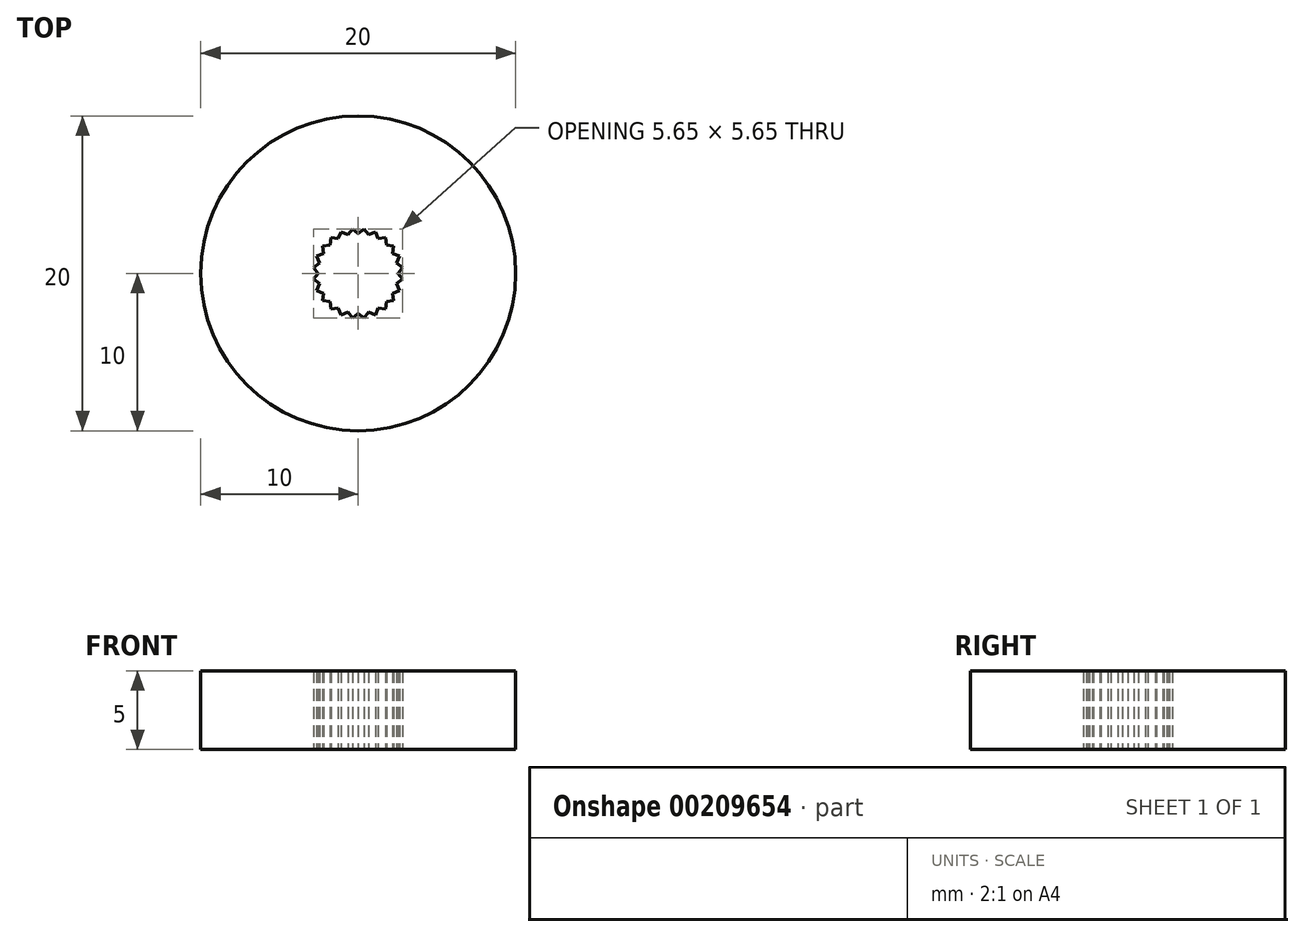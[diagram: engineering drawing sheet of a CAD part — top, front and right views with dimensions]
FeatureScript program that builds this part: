
annotation { "Feature Type Name" : "Feature", "Feature Type Description" : "" }
export const myFeature = defineFeature(function(context is Context, id is Id, definition is map)
    precondition{}
    {
        {
            var Q0;
            Q0=qCreatedBy(makeId("Top.planeOp"),FACE);
            var sketch = newSketch(context, id + "F0", { "sketchPlane" : qUnion([Q0])});
            skPoint(sketch, "E0", {"position": v(0, 2.54) * mm});
            skPoint(sketch, "E1", {"position": v(0.37, 2.83) * mm});
            skLineSegment(sketch, "E2", {"start": v(0, 2.54) * mm, "end": v(0.37, 2.83) * mm});
            skLineSegment(sketch, "E3", {"start": v(0, 2.54) * mm, "end": v(-0.37, 2.83) * mm});
            skLineSegment(sketch, "E4", {"start": v(0.37, 2.83) * mm, "end": v(0.66, 2.45) * mm});
            skLineSegment(sketch, "E5", {"start": v(0.66, 2.45) * mm, "end": v(1.1, 2.63) * mm});
            skLineSegment(sketch, "E6", {"start": v(1.27, 2.2) * mm, "end": v(1.1, 2.63) * mm});
            skLineSegment(sketch, "E7", {"start": v(1.73, 2.26) * mm, "end": v(1.27, 2.2) * mm});
            skLineSegment(sketch, "E8", {"start": v(1.8, 1.8) * mm, "end": v(1.73, 2.26) * mm});
            skLineSegment(sketch, "E9", {"start": v(2.26, 1.73) * mm, "end": v(1.8, 1.8) * mm});
            skLineSegment(sketch, "E10", {"start": v(2.2, 1.27) * mm, "end": v(2.26, 1.73) * mm});
            skLineSegment(sketch, "E11", {"start": v(2.2, 1.27) * mm, "end": v(2.63, 1.1) * mm});
            skLineSegment(sketch, "E12", {"start": v(2.63, 1.1) * mm, "end": v(2.45, 0.66) * mm});
            skLineSegment(sketch, "E13", {"start": v(2.45, 0.66) * mm, "end": v(2.83, 0.37) * mm});
            skLineSegment(sketch, "E14", {"start": v(2.83, 0.37) * mm, "end": v(2.54, 0) * mm});
            skLineSegment(sketch, "E15", {"start": v(2.54, 0) * mm, "end": v(2.83, -0.37) * mm});
            skLineSegment(sketch, "E16", {"start": v(2.83, -0.37) * mm, "end": v(2.45, -0.66) * mm});
            skLineSegment(sketch, "E17", {"start": v(2.45, -0.66) * mm, "end": v(2.63, -1.1) * mm});
            skLineSegment(sketch, "E18", {"start": v(2.63, -1.1) * mm, "end": v(2.2, -1.27) * mm});
            skLineSegment(sketch, "E19", {"start": v(2.2, -1.27) * mm, "end": v(2.26, -1.73) * mm});
            skLineSegment(sketch, "E20", {"start": v(2.26, -1.73) * mm, "end": v(1.8, -1.8) * mm});
            skLineSegment(sketch, "E21", {"start": v(1.8, -1.8) * mm, "end": v(1.73, -2.26) * mm});
            skLineSegment(sketch, "E22", {"start": v(1.73, -2.26) * mm, "end": v(1.27, -2.2) * mm});
            skLineSegment(sketch, "E23", {"start": v(1.27, -2.2) * mm, "end": v(1.1, -2.63) * mm});
            skLineSegment(sketch, "E24", {"start": v(1.1, -2.63) * mm, "end": v(0.66, -2.45) * mm});
            skLineSegment(sketch, "E25", {"start": v(0.66, -2.45) * mm, "end": v(0.37, -2.83) * mm});
            skLineSegment(sketch, "E26", {"start": v(0.37, -2.83) * mm, "end": v(0, -2.54) * mm});
            skLineSegment(sketch, "E27", {"start": v(0, -2.54) * mm, "end": v(-0.37, -2.83) * mm});
            skLineSegment(sketch, "E28", {"start": v(-0.37, -2.83) * mm, "end": v(-0.66, -2.45) * mm});
            skLineSegment(sketch, "E29", {"start": v(-0.66, -2.45) * mm, "end": v(-1.1, -2.63) * mm});
            skLineSegment(sketch, "E30", {"start": v(-1.1, -2.63) * mm, "end": v(-1.27, -2.2) * mm});
            skLineSegment(sketch, "E31", {"start": v(-1.27, -2.2) * mm, "end": v(-1.73, -2.26) * mm});
            skLineSegment(sketch, "E32", {"start": v(-1.73, -2.26) * mm, "end": v(-1.8, -1.8) * mm});
            skLineSegment(sketch, "E33", {"start": v(-1.8, -1.8) * mm, "end": v(-2.26, -1.73) * mm});
            skLineSegment(sketch, "E34", {"start": v(-2.26, -1.73) * mm, "end": v(-2.2, -1.27) * mm});
            skLineSegment(sketch, "E35", {"start": v(-2.63, -1.1) * mm, "end": v(-2.2, -1.27) * mm});
            skLineSegment(sketch, "E36", {"start": v(-2.63, -1.1) * mm, "end": v(-2.45, -0.66) * mm});
            skLineSegment(sketch, "E37", {"start": v(-2.45, -0.66) * mm, "end": v(-2.83, -0.37) * mm});
            skLineSegment(sketch, "E38", {"start": v(-2.83, -0.37) * mm, "end": v(-2.54, 0) * mm});
            skLineSegment(sketch, "E39", {"start": v(-2.54, 0) * mm, "end": v(-2.83, 0.37) * mm});
            skLineSegment(sketch, "E40", {"start": v(-2.83, 0.37) * mm, "end": v(-2.45, 0.66) * mm});
            skLineSegment(sketch, "E41", {"start": v(-2.63, 1.1) * mm, "end": v(-2.45, 0.66) * mm});
            skLineSegment(sketch, "E42", {"start": v(-2.2, 1.27) * mm, "end": v(-2.63, 1.1) * mm});
            skLineSegment(sketch, "E43", {"start": v(-2.26, 1.73) * mm, "end": v(-2.2, 1.27) * mm});
            skLineSegment(sketch, "E44", {"start": v(-2.26, 1.73) * mm, "end": v(-1.8, 1.8) * mm});
            skLineSegment(sketch, "E45", {"start": v(-1.8, 1.8) * mm, "end": v(-1.73, 2.26) * mm});
            skLineSegment(sketch, "E46", {"start": v(-1.73, 2.26) * mm, "end": v(-1.27, 2.2) * mm});
            skLineSegment(sketch, "E47", {"start": v(-1.27, 2.2) * mm, "end": v(-1.1, 2.63) * mm});
            skLineSegment(sketch, "E48", {"start": v(-1.1, 2.63) * mm, "end": v(-0.66, 2.45) * mm});
            skLineSegment(sketch, "E49", {"start": v(-0.66, 2.45) * mm, "end": v(-0.37, 2.83) * mm});
            skCircle(sketch, "E50", {"center": v(0, 0) * mm, "radius": 10 * mm});
            skSolve(sketch);
        }
        {
            var Q0;
            Q0=qSketchRegion(id+"F0",true);
            extrude(context, id + "F1", {"entities" : qUnion([Q0]), "depth" : 5 * mm});
        }
    });
